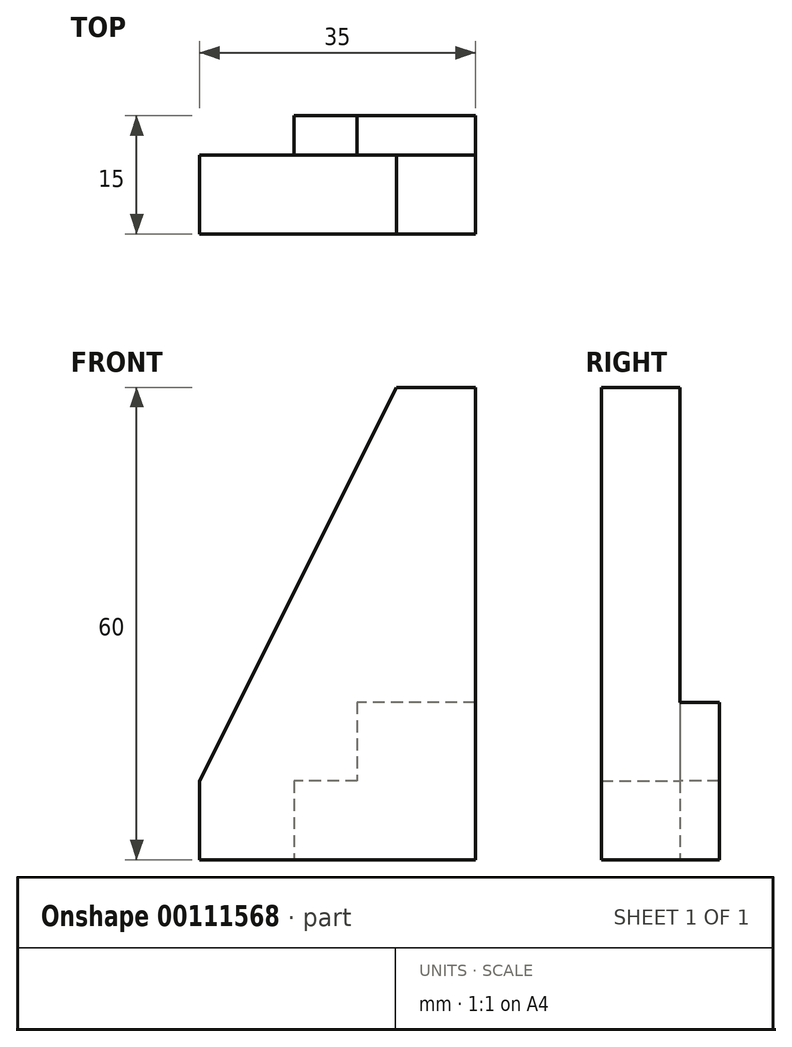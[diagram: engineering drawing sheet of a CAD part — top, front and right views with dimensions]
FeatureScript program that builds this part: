
annotation { "Feature Type Name" : "Feature", "Feature Type Description" : "" }
export const myFeature = defineFeature(function(context is Context, id is Id, definition is map)
    precondition{}
    {
        {
            var Q0;
            Q0=qCreatedBy(makeId("Front.planeOp"),FACE);
            var sketch = newSketch(context, id + "F0", { "sketchPlane" : qUnion([Q0])});
            skLineSegment(sketch, "E0", {"start": v(-19.1, 0) * mm, "end": v(-19.1, 60) * mm});
            skLineSegment(sketch, "E1", {"start": v(-19.1, 60) * mm, "end": v(-29.1, 60) * mm});
            skLineSegment(sketch, "E2", {"start": v(-29.1, 60) * mm, "end": v(-54.1, 10) * mm});
            skLineSegment(sketch, "E3", {"start": v(-54.1, 10) * mm, "end": v(-54.1, 0) * mm});
            skLineSegment(sketch, "E4", {"start": v(-54.1, 0) * mm, "end": v(-19.1, 0) * mm});
            skSolve(sketch);
        }
        {
            var Q0;
            Q0=qSketchRegion(id+"F0",true);
            var Q1;
            Q1=makeQuery(id+"F0.imprint","IMPRINT",FACE,{"disambiguationData":[TD([[makeQuery(id+"F0.imprint","IMPRINT",EDGE,{"derivedFrom":sQuery(id+"F0.wireOp",EDGE,"E0")}),1.0]])]});
            extrude(context, id + "F1", {"entities" : qUnion([Q0, Q1]), "depth" : 10 * mm});
        }
        {
            var Q0;
            Q0=makeQuery(id+"F1.opExtrude","CAP_FACE",FACE,{"disambiguationData":[OSD([sQuery(id+"F0.wireOp",EDGE,"E0"),sQuery(id+"F0.wireOp",EDGE,"E1"),sQuery(id+"F0.wireOp",EDGE,"E2"),sQuery(id+"F0.wireOp",EDGE,"E3"),sQuery(id+"F0.wireOp",EDGE,"E4")])],"isStart":true});
            var sketch = newSketch(context, id + "F2", { "sketchPlane" : qUnion([Q0])});
            skLineSegment(sketch, "E5", {"start": v(19.1, 20) * mm, "end": v(34.1, 20) * mm});
            skLineSegment(sketch, "E6", {"start": v(34.1, 20) * mm, "end": v(34.1, 10) * mm});
            skLineSegment(sketch, "E7", {"start": v(34.1, 10) * mm, "end": v(42.1, 10) * mm});
            skLineSegment(sketch, "E8", {"start": v(42.1, 10) * mm, "end": v(42.1, 0) * mm});
            skSolve(sketch);
        }
        {
            var Q0;
            {var subQ4=sQuery(id+"F2.wireOp",EDGE,"E5");Q0=makeQuery(id+"F2.imprint","IMPRINT",FACE,{"disambiguationData":[TD([[makeQuery(id+"F2.imprint","IMPRINT",EDGE,{"derivedFrom":subQ4}),-1.0]])]});}
            extrude(context, id + "F3", {"entities" : qUnion([Q0]), "operationType" : NewBodyOperationType.ADD, "depth" : 5 * mm});
        }
    });
